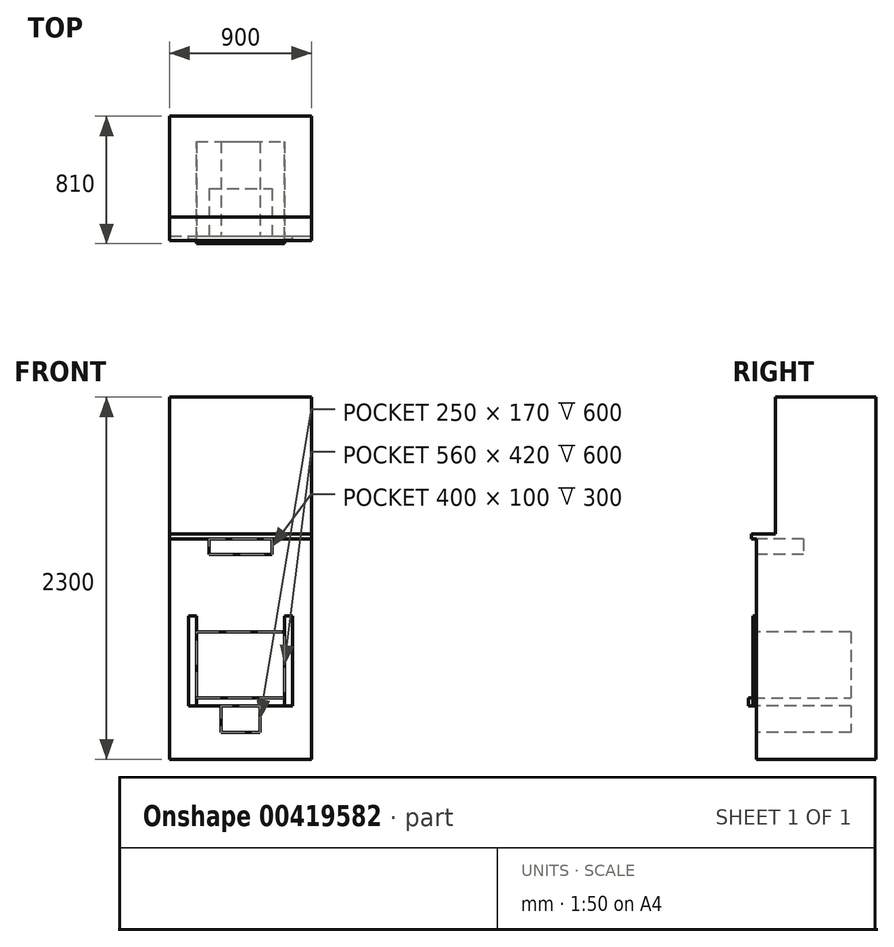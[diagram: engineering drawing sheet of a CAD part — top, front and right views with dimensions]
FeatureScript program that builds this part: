
annotation { "Feature Type Name" : "Feature", "Feature Type Description" : "" }
export const myFeature = defineFeature(function(context is Context, id is Id, definition is map)
    precondition{}
    {
        {
            var Q0;
            Q0=qCreatedBy(makeId("Top.planeOp"),FACE);
            var sketch = newSketch(context, id + "F0", { "sketchPlane" : qUnion([Q0])});
            skLineSegment(sketch, "E0.bottom", {"start": v(-622.57, 0) * mm, "end": v(277.43, 0) * mm});
            skLineSegment(sketch, "E0.top", {"start": v(-622.57, -760) * mm, "end": v(277.43, -760) * mm});
            skLineSegment(sketch, "E0.left", {"start": v(-622.57, 0) * mm, "end": v(-622.57, -760) * mm});
            skLineSegment(sketch, "E0.right", {"start": v(277.43, 0) * mm, "end": v(277.43, -760) * mm});
            skSolve(sketch);
        }
        {
            var Q0;
            Q0 = qSketchRegion(id + "F0", true);
            extrude(context, id + "F1", {"entities" : qUnion([Q0]), "depth" : 1400 * mm});
        }
        {
            var Q0;
            Q0=makeQuery(id+"F1.opExtrude","CAP_FACE",FACE,{"disambiguationData":[OSD([sQuery(id+"F0.wireOp",EDGE,"E0.bottom"),sQuery(id+"F0.wireOp",EDGE,"E0.top"),sQuery(id+"F0.wireOp",EDGE,"E0.left"),sQuery(id+"F0.wireOp",EDGE,"E0.right")])],"isStart":false});
            var sketch = newSketch(context, id + "F2", { "sketchPlane" : qUnion([Q0])});
            skLineSegment(sketch, "E1.0", {"start": v(-622.57, -640) * mm, "end": v(277.43, -640) * mm});
            skSolve(sketch);
        }
        {
            var Q0;
            {var subQ0=sQuery(id+"F2.wireOp",EDGE,"E1.0");Q0=makeQuery(id+"F2.imprint","IMPRINT",FACE,{"disambiguationData":[TD([[makeQuery(id+"F2.imprint","IMPRINT",EDGE,{"derivedFrom":subQ0}),1.0]])]});}
            extrude(context, id + "F3", {"entities" : qUnion([Q0]), "operationType" : NewBodyOperationType.ADD, "depth" : 900 * mm});
        }
        {
            var Q0;
            Q0=makeQuery(id+"F1.opExtrude","CAP_FACE",FACE,{"disambiguationData":[OSD([sQuery(id+"F0.wireOp",EDGE,"E0.bottom"),sQuery(id+"F0.wireOp",EDGE,"E0.top"),sQuery(id+"F0.wireOp",EDGE,"E0.left"),sQuery(id+"F0.wireOp",EDGE,"E0.right")])],"isStart":false});
            var sketch = newSketch(context, id + "F4", { "sketchPlane" : qUnion([Q0])});
            skLineSegment(sketch, "E2.0", {"start": v(-622.57, -790) * mm, "end": v(277.43, -790) * mm});
            skLineSegment(sketch, "E3", {"start": v(277.43, -790) * mm, "end": v(277.43, -640) * mm});
            skLineSegment(sketch, "E4", {"start": v(-622.57, -790) * mm, "end": v(-622.57, -640) * mm});
            skSolve(sketch);
        }
        {
            var Q0;
            Q0 = qSketchRegion(id + "F4", true);
            var Q1;
            {var subQ1=makeQuery(id+"F1.opExtrude","CAP_EDGE",EDGE,{"disambiguationData":[OSD([sQuery(id+"F0.wireOp",EDGE,"E0.top")])],"isStart":false});Q1=makeQuery(id+"F4.imprint","IMPRINT",FACE,{"disambiguationData":[TD([[makeQuery(id+"F4.imprint","IMPRINT",EDGE,{"derivedFrom":subQ1}),1.0]])]});}
            var Q2;
            {var subQ0=sQuery(id+"F4.wireOp",EDGE,"E2.0");Q2=makeQuery(id+"F4.imprint","IMPRINT",FACE,{"disambiguationData":[TD([[makeQuery(id+"F4.imprint","IMPRINT",EDGE,{"derivedFrom":subQ0}),1.0]])]});}
            extrude(context, id + "F5", {"entities" : qUnion([Q0, Q1, Q2]), "operationType" : NewBodyOperationType.ADD, "depth" : 30 * mm});
        }
        {
            var Q0;
            Q0=makeQuery(id+"F1.opExtrude","SWEPT_FACE",FACE,{"disambiguationData":[OSD([sQuery(id+"F0.wireOp",EDGE,"E0.top")])]});
            var sketch = newSketch(context, id + "F6", { "sketchPlane" : qUnion([Q0])});
            skLineSegment(sketch, "E5.0", {"start": v(-452.57, 390) * mm, "end": v(107.43, 390) * mm});
            skLineSegment(sketch, "E6.0", {"start": v(-452.57, 810) * mm, "end": v(107.43, 810) * mm});
            skLineSegment(sketch, "E7.0", {"start": v(107.43, 910) * mm, "end": v(107.43, 340) * mm});
            skLineSegment(sketch, "E8.0", {"start": v(-452.57, 910) * mm, "end": v(-452.57, 340) * mm});
            skLineSegment(sketch, "E9.0", {"start": v(-502.57, 910) * mm, "end": v(157.43, 910) * mm});
            skLineSegment(sketch, "E10.0", {"start": v(-502.57, 340) * mm, "end": v(157.43, 340) * mm});
            skLineSegment(sketch, "E11.0", {"start": v(-502.57, 910) * mm, "end": v(-502.57, 340) * mm});
            skLineSegment(sketch, "E12.0", {"start": v(157.43, 910) * mm, "end": v(157.43, 340) * mm});
            skLineSegment(sketch, "E13.0", {"start": v(-297.57, 170) * mm, "end": v(-47.57, 170) * mm});
            skLineSegment(sketch, "E14.0", {"start": v(-297.57, 340) * mm, "end": v(-297.57, 170) * mm});
            skLineSegment(sketch, "E15.0", {"start": v(-47.57, 340) * mm, "end": v(-47.57, 170) * mm});
            skLineSegment(sketch, "E16.0", {"start": v(-372.57, 1300) * mm, "end": v(27.43, 1300) * mm});
            skLineSegment(sketch, "E17.0", {"start": v(-372.57, 1400) * mm, "end": v(-372.57, 1300) * mm});
            skLineSegment(sketch, "E18.0", {"start": v(27.43, 1400) * mm, "end": v(27.43, 1300) * mm});
            skSolve(sketch);
        }
        {
            var Q0;
            {var subQ3=sQuery(id+"F6.wireOp",EDGE,"E11.0");Q0=makeQuery(id+"F6.imprint","IMPRINT",FACE,{"disambiguationData":[TD([[makeQuery(id+"F6.imprint","IMPRINT",EDGE,{"derivedFrom":subQ3}),1.0]])]});}
            var Q1;
            {var subQ3=sQuery(id+"F6.wireOp",EDGE,"E12.0");Q1=makeQuery(id+"F6.imprint","IMPRINT",FACE,{"disambiguationData":[TD([[makeQuery(id+"F6.imprint","IMPRINT",EDGE,{"derivedFrom":subQ3}),-1.0]])]});}
            extrude(context, id + "F7", {"entities" : qUnion([Q0, Q1]), "operationType" : NewBodyOperationType.ADD, "depth" : 20 * mm});
        }
        {
            var Q0;
            Q0=makeQuery(id+"F1.opExtrude","SWEPT_FACE",FACE,{"disambiguationData":[OSD([sQuery(id+"F0.wireOp",EDGE,"E0.top")])]});
            var sketch = newSketch(context, id + "F8", { "sketchPlane" : qUnion([Q0])});
            skLineSegment(sketch, "E19.0", {"start": v(-452.57, 390) * mm, "end": v(107.43, 390) * mm});
            skLineSegment(sketch, "E20", {"start": v(-452.57, 340) * mm, "end": v(-452.57, 390) * mm});
            skLineSegment(sketch, "E21", {"start": v(107.43, 340) * mm, "end": v(107.43, 390) * mm});
            skLineSegment(sketch, "E22.0", {"start": v(-452.57, 340) * mm, "end": v(107.43, 340) * mm});
            skSolve(sketch);
        }
        {
            var Q0;
            Q0=makeQuery(id+"F8.imprint","IMPRINT",FACE,{"disambiguationData":[TD([[makeQuery(id+"F8.imprint","IMPRINT",EDGE,{"derivedFrom":sQuery(id+"F8.wireOp",EDGE,"E19.0")}),-1.0]])]});
            extrude(context, id + "F9", {"entities" : qUnion([Q0]), "operationType" : NewBodyOperationType.ADD, "depth" : 50 * mm});
        }
        {
            var Q0;
            Q0=makeQuery(id+"F1.opExtrude","SWEPT_FACE",FACE,{"disambiguationData":[OSD([sQuery(id+"F0.wireOp",EDGE,"E0.top")])]});
            var sketch = newSketch(context, id + "F10", { "sketchPlane" : qUnion([Q0])});
            skLineSegment(sketch, "E23.0", {"start": v(-297.57, 170) * mm, "end": v(-47.57, 170) * mm});
            skLineSegment(sketch, "E24.0", {"start": v(-297.57, 340) * mm, "end": v(-297.57, 170) * mm});
            skLineSegment(sketch, "E25.0", {"start": v(-47.57, 340) * mm, "end": v(-47.57, 170) * mm});
            skLineSegment(sketch, "E26.0", {"start": v(-297.57, 340) * mm, "end": v(-47.57, 340) * mm});
            skSolve(sketch);
        }
        {
            var Q0;
            Q0=makeQuery(id+"F10.imprint","IMPRINT",FACE,{"disambiguationData":[TD([[makeQuery(id+"F10.imprint","IMPRINT",EDGE,{"derivedFrom":sQuery(id+"F10.wireOp",EDGE,"E23.0")}),1.0]])]});
            extrude(context, id + "F11", {"entities" : qUnion([Q0]), "operationType" : NewBodyOperationType.REMOVE, "oppositeDirection" : true, "depth" : 600 * mm});
        }
        {
            var Q0;
            Q0=makeQuery(id+"F1.opExtrude","SWEPT_FACE",FACE,{"disambiguationData":[OSD([sQuery(id+"F0.wireOp",EDGE,"E0.top")])]});
            var sketch = newSketch(context, id + "F12", { "sketchPlane" : qUnion([Q0])});
            skLineSegment(sketch, "E27.0", {"start": v(-452.57, 810) * mm, "end": v(107.43, 810) * mm});
            skSolve(sketch);
        }
        {
            var Q0;
            {var subQ0=sQuery(id+"F12.wireOp",EDGE,"E27.0");Q0=makeQuery(id+"F12.imprint","IMPRINT",FACE,{"disambiguationData":[TD([[makeQuery(id+"F12.imprint","IMPRINT",EDGE,{"derivedFrom":subQ0}),-1.0]])]});}
            extrude(context, id + "F13", {"entities" : qUnion([Q0]), "operationType" : NewBodyOperationType.REMOVE, "oppositeDirection" : true, "depth" : 600 * mm});
        }
        {
            var Q0;
            Q0=makeQuery(id+"F1.opExtrude","SWEPT_FACE",FACE,{"disambiguationData":[OSD([sQuery(id+"F0.wireOp",EDGE,"E0.top")])]});
            var sketch = newSketch(context, id + "F14", { "sketchPlane" : qUnion([Q0])});
            skLineSegment(sketch, "E28.0", {"start": v(-372.57, 1300) * mm, "end": v(27.43, 1300) * mm});
            skLineSegment(sketch, "E29.0", {"start": v(-372.57, 1400) * mm, "end": v(-372.57, 1300) * mm});
            skLineSegment(sketch, "E30.0", {"start": v(27.43, 1400) * mm, "end": v(27.43, 1300) * mm});
            skSolve(sketch);
        }
        {
            var Q0;
            Q0=makeQuery(id+"F14.imprint","IMPRINT",FACE,{"disambiguationData":[TD([[makeQuery(id+"F14.imprint","IMPRINT",EDGE,{"derivedFrom":sQuery(id+"F14.wireOp",EDGE,"E28.0")}),1.0]])]});
            extrude(context, id + "F15", {"entities" : qUnion([Q0]), "operationType" : NewBodyOperationType.REMOVE, "oppositeDirection" : true, "depth" : 300 * mm});
        }
    });
